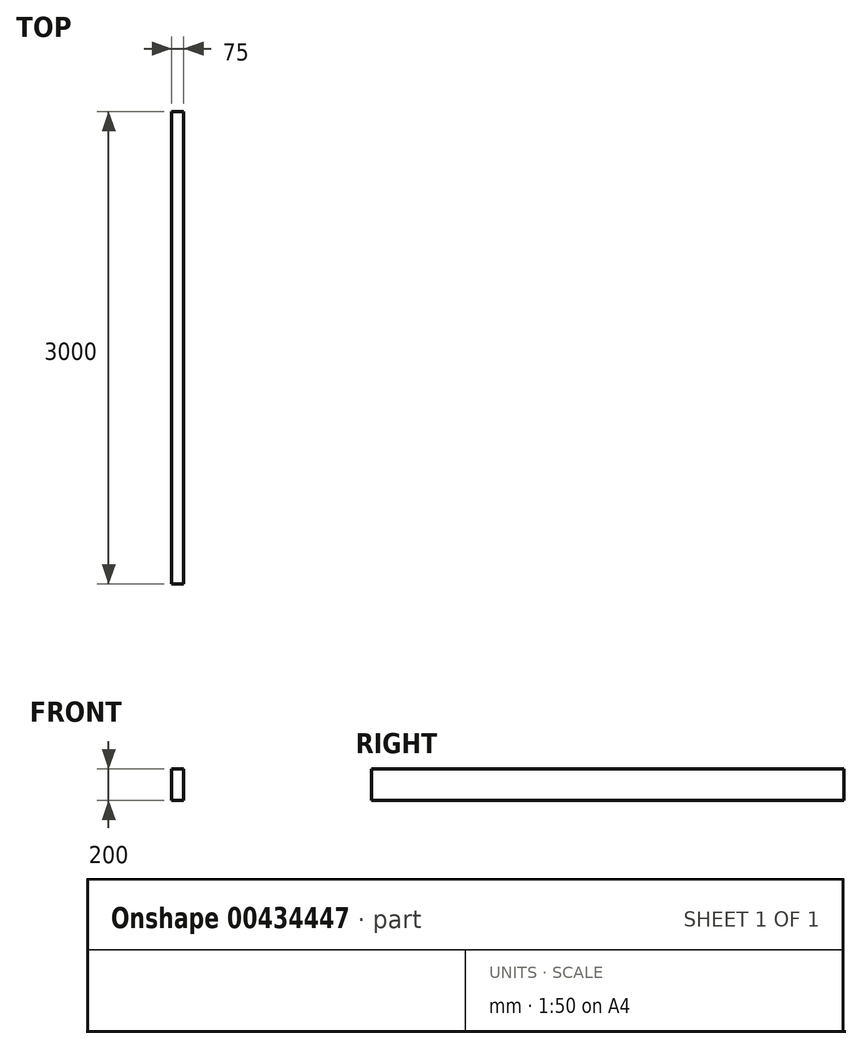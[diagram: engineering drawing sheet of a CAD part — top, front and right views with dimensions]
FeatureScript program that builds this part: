
annotation { "Feature Type Name" : "Feature", "Feature Type Description" : "" }
export const myFeature = defineFeature(function(context is Context, id is Id, definition is map)
    precondition{}
    {
        {
            var Q0;
            Q0=qCreatedBy(makeId("Front.planeOp"),FACE);
            var sketch = newSketch(context, id + "F0", { "sketchPlane" : qUnion([Q0])});
            skLineSegment(sketch, "E0.bottom", {"start": v(37.5, 100) * mm, "end": v(-37.5, 100) * mm});
            skLineSegment(sketch, "E0.top", {"start": v(37.5, -100) * mm, "end": v(-37.5, -100) * mm});
            skLineSegment(sketch, "E0.left", {"start": v(37.5, 100) * mm, "end": v(37.5, -100) * mm});
            skLineSegment(sketch, "E0.right", {"start": v(-37.5, 100) * mm, "end": v(-37.5, -100) * mm});
            skPoint(sketch, "E0.middle", {"position": v(0, 0) * mm});
            skSolve(sketch);
        }
        {
            var Q0;
            Q0 = qSketchRegion(id + "F0", true);
            extrude(context, id + "F1", {"entities" : qUnion([Q0]), "depth" : 3000 * mm, "offsetDistance" : 25 * mm});
        }
    });
